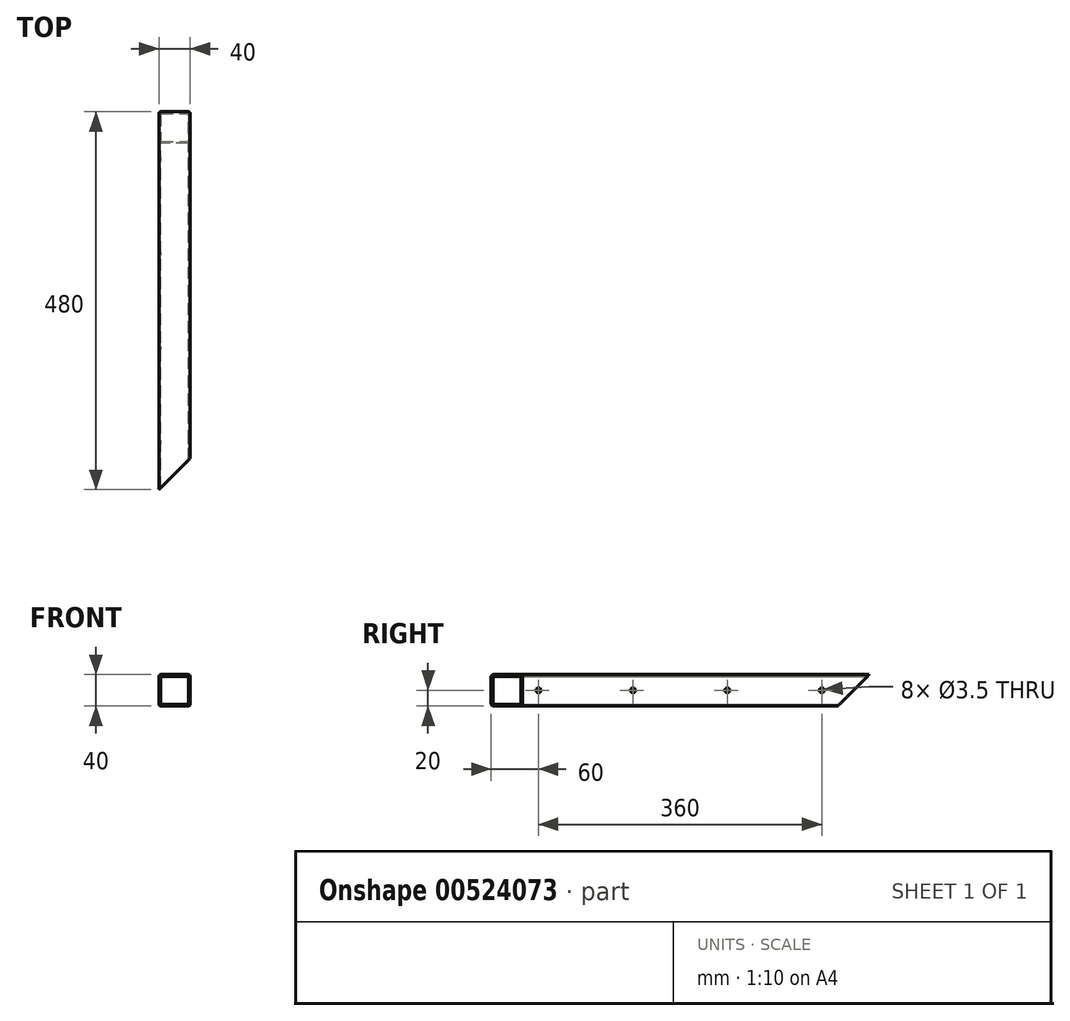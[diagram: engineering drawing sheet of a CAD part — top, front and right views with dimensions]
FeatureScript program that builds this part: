
annotation { "Feature Type Name" : "Feature", "Feature Type Description" : "" }
export const myFeature = defineFeature(function(context is Context, id is Id, definition is map)
    precondition{}
    {
        {
            assignVariable(context, id + "F0", {"name" : "R", "anyValue" : 3});
        }
        {
            assignVariable(context, id + "F1", {"name" : "W", "anyValue" : 2});
        }
        {
            var Q0;
            Q0=qCreatedBy(makeId("Front.planeOp"),FACE);
            var sketch = newSketch(context, id + "F2", { "sketchPlane" : qUnion([Q0])});
            skLineSegment(sketch, "E0.bottom", {"start": v(-20, 20) * mm, "end": v(20, 20) * mm});
            skLineSegment(sketch, "E0.top", {"start": v(-20, -20) * mm, "end": v(20, -20) * mm});
            skLineSegment(sketch, "E0.left", {"start": v(-20, 20) * mm, "end": v(-20, -20) * mm});
            skLineSegment(sketch, "E0.right", {"start": v(20, 20) * mm, "end": v(20, -20) * mm});
            skSolve(sketch);
        }
        {
            var Q0;
            Q0=qSketchRegion(id+"F2",true);
            extrude(context, id + "F3", {"entities" : qUnion([Q0]), "endBound" : BoundingType.SYMMETRIC, "depth" : 480 * mm, "offsetDistance" : 25 * mm});
        }
        {
            var Q0;
            Q0=makeQuery(id+"F3.opExtrude","SWEPT_EDGE",EDGE,{"disambiguationData":[OSD([sQuery(id+"F2.wireOp",EDGE,"E0.bottom"),sQuery(id+"F2.wireOp",EDGE,"E0.right")])]});
            var Q1;
            Q1=makeQuery(id+"F3.opExtrude","SWEPT_EDGE",EDGE,{"disambiguationData":[OSD([sQuery(id+"F2.wireOp",EDGE,"E0.bottom"),sQuery(id+"F2.wireOp",EDGE,"E0.left")])]});
            var Q2;
            Q2=makeQuery(id+"F3.opExtrude","SWEPT_EDGE",EDGE,{"disambiguationData":[OSD([sQuery(id+"F2.wireOp",EDGE,"E0.top"),sQuery(id+"F2.wireOp",EDGE,"E0.right")])]});
            var Q3;
            Q3=makeQuery(id+"F3.opExtrude","SWEPT_EDGE",EDGE,{"disambiguationData":[OSD([sQuery(id+"F2.wireOp",EDGE,"E0.top"),sQuery(id+"F2.wireOp",EDGE,"E0.left")])]});
            fillet(context, id + "F4", {"entities" : qUnion([Q0, Q1, Q2, Q3]), "radius" : (getVariable(context, 'R')) * mm, "tangentPropagation" : true, "allowEdgeOverflow" : false});
        }
        {
            var Q0;
            Q0=makeQuery(id+"F3.opExtrude","CAP_FACE",FACE,{"disambiguationData":[OSD([sQuery(id+"F2.wireOp",EDGE,"E0.bottom"),sQuery(id+"F2.wireOp",EDGE,"E0.top"),sQuery(id+"F2.wireOp",EDGE,"E0.left"),sQuery(id+"F2.wireOp",EDGE,"E0.right")])],"isStart":false});
            var Q1;
            Q1=makeQuery(id+"F3.opExtrude","CAP_FACE",FACE,{"disambiguationData":[OSD([sQuery(id+"F2.wireOp",EDGE,"E0.bottom"),sQuery(id+"F2.wireOp",EDGE,"E0.top"),sQuery(id+"F2.wireOp",EDGE,"E0.left"),sQuery(id+"F2.wireOp",EDGE,"E0.right")])],"isStart":true});
            shell(context, id + "F5", {"entities" : qUnion([Q0, Q1]), "thickness" : (getVariable(context, 'W')) * mm});
        }
        {
            var Q0;
            Q0=makeQuery(id+"F3.opExtrude","SWEPT_FACE",FACE,{"disambiguationData":[OSD([sQuery(id+"F2.wireOp",EDGE,"E0.left")])]});
            var sketch = newSketch(context, id + "F6", { "sketchPlane" : qUnion([Q0])});
            skLineSegment(sketch, "E1", {"start": v(-240, -20) * mm, "end": v(-200, -20) * mm});
            skLineSegment(sketch, "E2", {"start": v(-200, -20) * mm, "end": v(-240, 20) * mm});
            skLineSegment(sketch, "E3", {"start": v(-240, 20) * mm, "end": v(-240, -20) * mm});
            skSolve(sketch);
        }
        {
            var Q0;
            Q0=qSketchRegion(id+"F6",true);
            extrude(context, id + "F7", {"entities" : qUnion([Q0]), "operationType" : NewBodyOperationType.REMOVE, "endBound" : BoundingType.THROUGH_ALL, "oppositeDirection" : true, "depth" : 25 * mm, "offsetDistance" : 25 * mm});
        }
        {
            var Q0;
            Q0=makeQuery(id+"F3.opExtrude","SWEPT_FACE",FACE,{"disambiguationData":[OSD([sQuery(id+"F2.wireOp",EDGE,"E0.bottom")])]});
            var sketch = newSketch(context, id + "F8", { "sketchPlane" : qUnion([Q0])});
            skLineSegment(sketch, "E4.0", {"start": v(20, 237) * mm, "end": v(20, -240) * mm, "construction": true});
            skLineSegment(sketch, "E5", {"start": v(20, -200) * mm, "end": v(-20, -240) * mm});
            skLineSegment(sketch, "E6", {"start": v(-20, -240) * mm, "end": v(20, -240) * mm});
            skLineSegment(sketch, "E7", {"start": v(20, -200) * mm, "end": v(20, -240) * mm});
            skSolve(sketch);
        }
        {
            var Q0;
            Q0=qSketchRegion(id+"F8",true);
            extrude(context, id + "F9", {"entities" : qUnion([Q0]), "operationType" : NewBodyOperationType.REMOVE, "endBound" : BoundingType.THROUGH_ALL, "oppositeDirection" : true, "depth" : 25 * mm, "offsetDistance" : 25 * mm});
        }
        {
            var Q0;
            Q0=makeQuery(id+"F3.opExtrude","SWEPT_FACE",FACE,{"disambiguationData":[OSD([sQuery(id+"F2.wireOp",EDGE,"E0.right")])]});
            var sketch = newSketch(context, id + "F10", { "sketchPlane" : qUnion([Q0])});
            skPoint(sketch, "E8", {"position": v(180, 0) * mm});
            skPoint(sketch, "E9", {"position": v(60, 0) * mm});
            skPoint(sketch, "E10", {"position": v(-60, 0) * mm});
            skPoint(sketch, "E11", {"position": v(-180, 0) * mm});
            skSolve(sketch);
        }
        {
            var Q0;
            Q0=sQuery(id+"F10.wireOp",VERTEX,"E8");
            var Q1;
            Q1=sQuery(id+"F10.wireOp",VERTEX,"E9");
            var Q2;
            Q2=sQuery(id+"F10.wireOp",VERTEX,"E10");
            var Q3;
            Q3=sQuery(id+"F10.wireOp",VERTEX,"E11");
            var Q4;
            Q4=makeQuery(id+"F3.opExtrude","SWEPT_BODY",BODY,{"disambiguationData":[OSD([sQuery(id+"F2.wireOp",EDGE,"E0.bottom"),sQuery(id+"F2.wireOp",EDGE,"E0.top"),sQuery(id+"F2.wireOp",EDGE,"E0.left"),sQuery(id+"F2.wireOp",EDGE,"E0.right")])]});
            hole(context, id + "F11", {"style" : HoleStyle.C_SINK, "endStyle" : HoleEndStyle.THROUGH, "holeDiameter" : 3.5 * mm, "cSinkDiameter" : 6 * mm, "cSinkAngle" : 90 * degree, "isTappedThrough" : true, "tappedDepth" : 12 * mm, "tapClearance" : 3, "locations" : qUnion([Q0, Q1, Q2, Q3]), "scope" : qUnion([Q4])});
        }
    });
